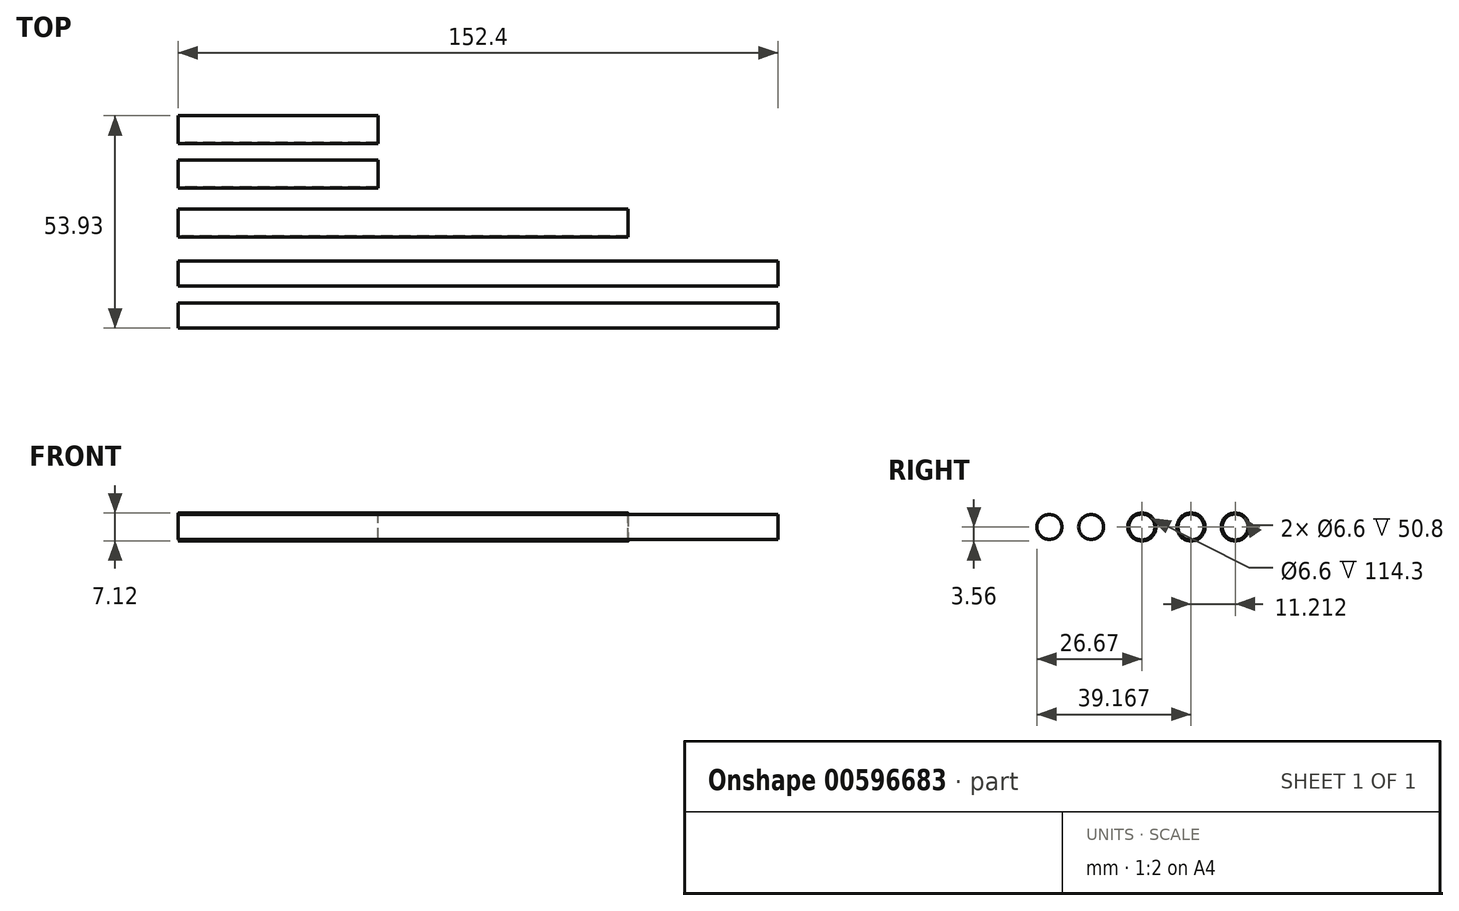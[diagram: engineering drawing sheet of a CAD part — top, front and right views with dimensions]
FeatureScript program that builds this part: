
annotation { "Feature Type Name" : "Feature", "Feature Type Description" : "" }
export const myFeature = defineFeature(function(context is Context, id is Id, definition is map)
    precondition{}
    {
        {
            var Q0;
            Q0=qCreatedBy(makeId("Right.planeOp"),FACE);
            var sketch = newSketch(context, id + "F0", { "sketchPlane" : qUnion([Q0])});
            skCircle(sketch, "E0", {"center": v(0, 0) * mm, "radius": 3.56 * mm});
            skCircle(sketch, "E1", {"center": v(12.5, 0) * mm, "radius": 3.56 * mm});
            skCircle(sketch, "E2", {"center": v(-12.88, 0) * mm, "radius": 3.18 * mm});
            skCircle(sketch, "E3", {"center": v(-23.5, 0) * mm, "radius": 3.18 * mm});
            skCircle(sketch, "E4", {"center": v(23.7, 0) * mm, "radius": 3.56 * mm});
            skCircle(sketch, "E5", {"center": v(0, 0) * mm, "radius": 3.3 * mm});
            skCircle(sketch, "E6", {"center": v(12.5, 0) * mm, "radius": 3.3 * mm});
            skCircle(sketch, "E7", {"center": v(23.7, 0) * mm, "radius": 3.3 * mm});
            skSolve(sketch);
        }
        {
            var Q0;
            Q0 = qSketchRegion(id + "F0", true);
            extrude(context, id + "F1", {"entities" : qUnion([Q0]), "depth" : 152.4 * mm, "offsetDistance" : 25.4 * mm});
        }
        {
            var Q0;
            Q0=makeQuery(id+"F1.opExtrude","CAP_FACE",FACE,{"disambiguationData":[OSD([sQuery(id+"F0.wireOp",EDGE,"E4"),sQuery(id+"F0.wireOp",EDGE,"E7")])],"isStart":false});
            extrude(context, id + "F2", {"entities" : qUnion([Q0]), "operationType" : NewBodyOperationType.REMOVE, "oppositeDirection" : true, "depth" : 101.6 * mm, "offsetDistance" : 25.4 * mm});
        }
        {
            var Q0;
            Q0=makeQuery(id+"F1.opExtrude","CAP_FACE",FACE,{"disambiguationData":[OSD([sQuery(id+"F0.wireOp",EDGE,"E1"),sQuery(id+"F0.wireOp",EDGE,"E6")])],"isStart":false});
            extrude(context, id + "F3", {"entities" : qUnion([Q0]), "operationType" : NewBodyOperationType.REMOVE, "oppositeDirection" : true, "depth" : 101.6 * mm, "offsetDistance" : 25.4 * mm});
        }
        {
            var Q0;
            Q0=makeQuery(id+"F1.opExtrude","CAP_FACE",FACE,{"disambiguationData":[OSD([sQuery(id+"F0.wireOp",EDGE,"E0"),sQuery(id+"F0.wireOp",EDGE,"E5")])],"isStart":false});
            extrude(context, id + "F4", {"entities" : qUnion([Q0]), "operationType" : NewBodyOperationType.REMOVE, "oppositeDirection" : true, "depth" : 38.1 * mm, "offsetDistance" : 25.4 * mm});
        }
    });
